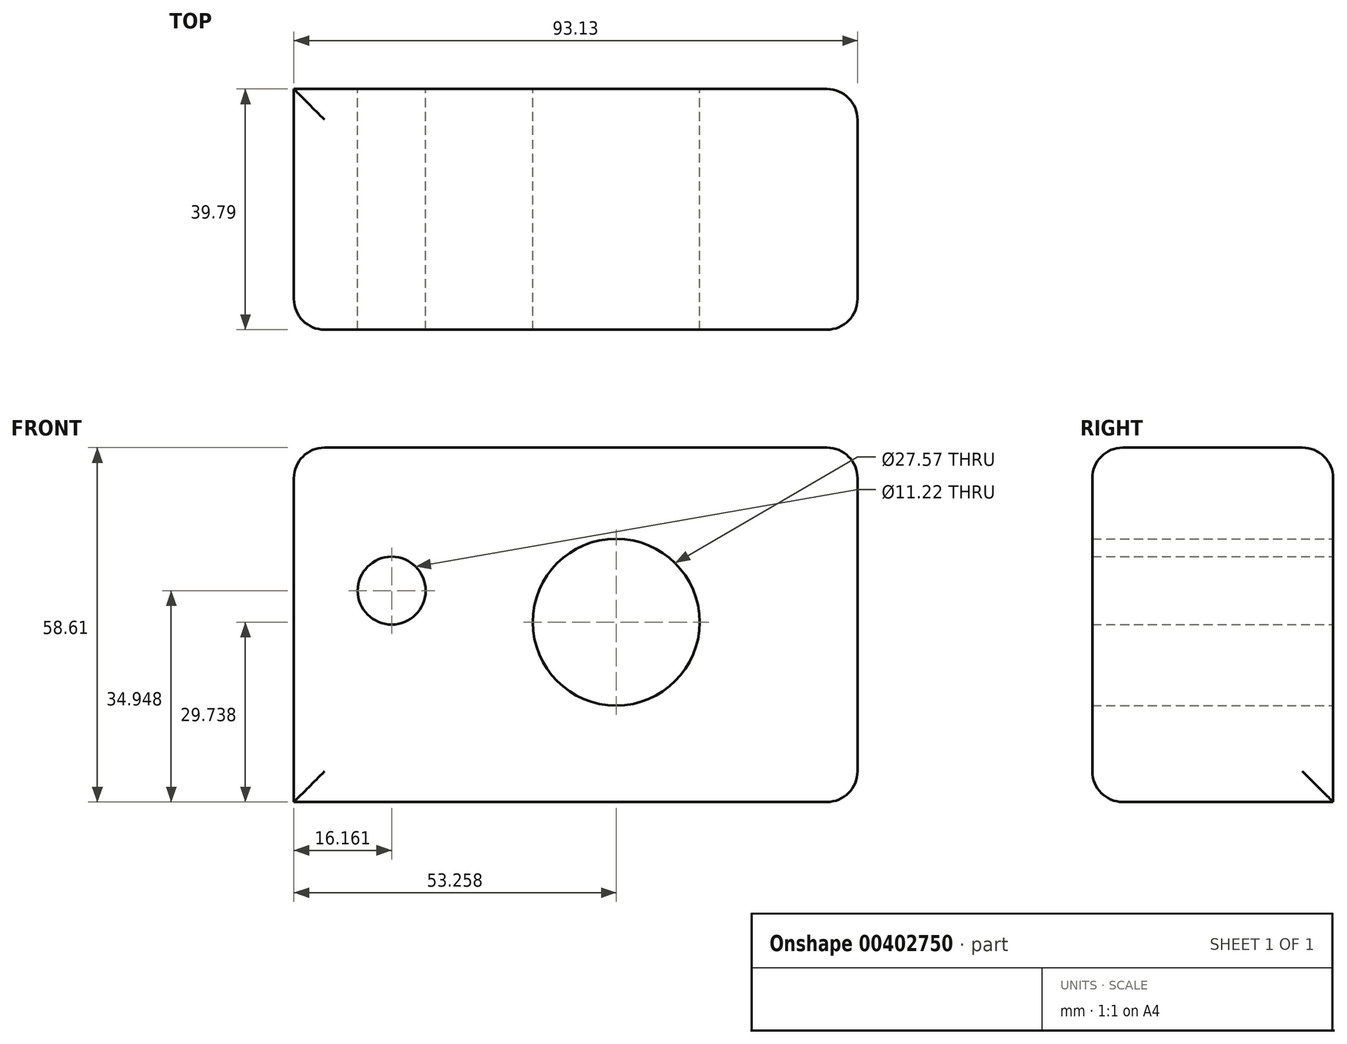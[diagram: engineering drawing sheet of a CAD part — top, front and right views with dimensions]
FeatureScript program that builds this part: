
annotation { "Feature Type Name" : "Feature", "Feature Type Description" : "" }
export const myFeature = defineFeature(function(context is Context, id is Id, definition is map)
    precondition{}
    {
        {
            var Q0;
            Q0=qCreatedBy(makeId("Front.planeOp"),FACE);
            var sketch = newSketch(context, id + "F0", { "sketchPlane" : qUnion([Q0])});
            skLineSegment(sketch, "E0.bottom", {"start": v(0, 0) * mm, "end": v(93.13, 0) * mm});
            skLineSegment(sketch, "E0.top", {"start": v(0, 58.6) * mm, "end": v(93.13, 58.6) * mm});
            skLineSegment(sketch, "E0.left", {"start": v(0, 0) * mm, "end": v(0, 58.6) * mm});
            skLineSegment(sketch, "E0.right", {"start": v(93.13, 0) * mm, "end": v(93.13, 58.6) * mm});
            skCircle(sketch, "E1", {"center": v(53.26, 29.74) * mm, "radius": 13.79 * mm});
            skCircle(sketch, "E2", {"center": v(16.16, 34.95) * mm, "radius": 5.6 * mm});
            skSolve(sketch);
        }
        {
            var Q0;
            Q0=makeQuery(id+"F0.imprint","IMPRINT",FACE,{"disambiguationData":[TD([[makeQuery(id+"F0.imprint","IMPRINT",EDGE,{"derivedFrom":sQuery(id+"F0.wireOp",EDGE,"E0.bottom")}),1.0]])]});
            extrude(context, id + "F1", {"entities" : qUnion([Q0]), "depth" : 39.8 * mm});
        }
        {
            var Q0;
            Q0=makeQuery(id+"F1.opExtrude","CAP_EDGE",EDGE,{"disambiguationData":[OSD([sQuery(id+"F0.wireOp",EDGE,"E0.top")])],"isStart":false});
            var Q1;
            Q1=makeQuery(id+"F1.opExtrude","CAP_EDGE",EDGE,{"disambiguationData":[OSD([sQuery(id+"F0.wireOp",EDGE,"E0.top")])],"isStart":true});
            var Q2;
            Q2=makeQuery(id+"F1.opExtrude","SWEPT_EDGE",EDGE,{"disambiguationData":[OSD([sQuery(id+"F0.wireOp",EDGE,"E0.top"),sQuery(id+"F0.wireOp",EDGE,"E0.left")])]});
            var Q3;
            Q3=makeQuery(id+"F1.opExtrude","SWEPT_EDGE",EDGE,{"disambiguationData":[OSD([sQuery(id+"F0.wireOp",EDGE,"E0.top"),sQuery(id+"F0.wireOp",EDGE,"E0.right")])]});
            var Q4;
            Q4=makeQuery(id+"F1.opExtrude","CAP_EDGE",EDGE,{"disambiguationData":[OSD([sQuery(id+"F0.wireOp",EDGE,"E0.right")])],"isStart":false});
            var Q5;
            Q5=makeQuery(id+"F1.opExtrude","CAP_EDGE",EDGE,{"disambiguationData":[OSD([sQuery(id+"F0.wireOp",EDGE,"E0.left")])],"isStart":false});
            var Q6;
            Q6=makeQuery(id+"F1.opExtrude","CAP_EDGE",EDGE,{"disambiguationData":[OSD([sQuery(id+"F0.wireOp",EDGE,"E0.bottom")])],"isStart":false});
            var Q7;
            Q7=makeQuery(id+"F1.opExtrude","CAP_EDGE",EDGE,{"disambiguationData":[OSD([sQuery(id+"F0.wireOp",EDGE,"E0.right")])],"isStart":true});
            var Q8;
            Q8=makeQuery(id+"F1.opExtrude","SWEPT_EDGE",EDGE,{"disambiguationData":[OSD([sQuery(id+"F0.wireOp",EDGE,"E0.bottom"),sQuery(id+"F0.wireOp",EDGE,"E0.right")])]});
            fillet(context, id + "F2", {"entities" : qUnion([Q0, Q1, Q2, Q3, Q4, Q5, Q6, Q7, Q8]), "radius" : 5.08 * mm, "tangentPropagation" : true, "allowEdgeOverflow" : false});
        }
    });
